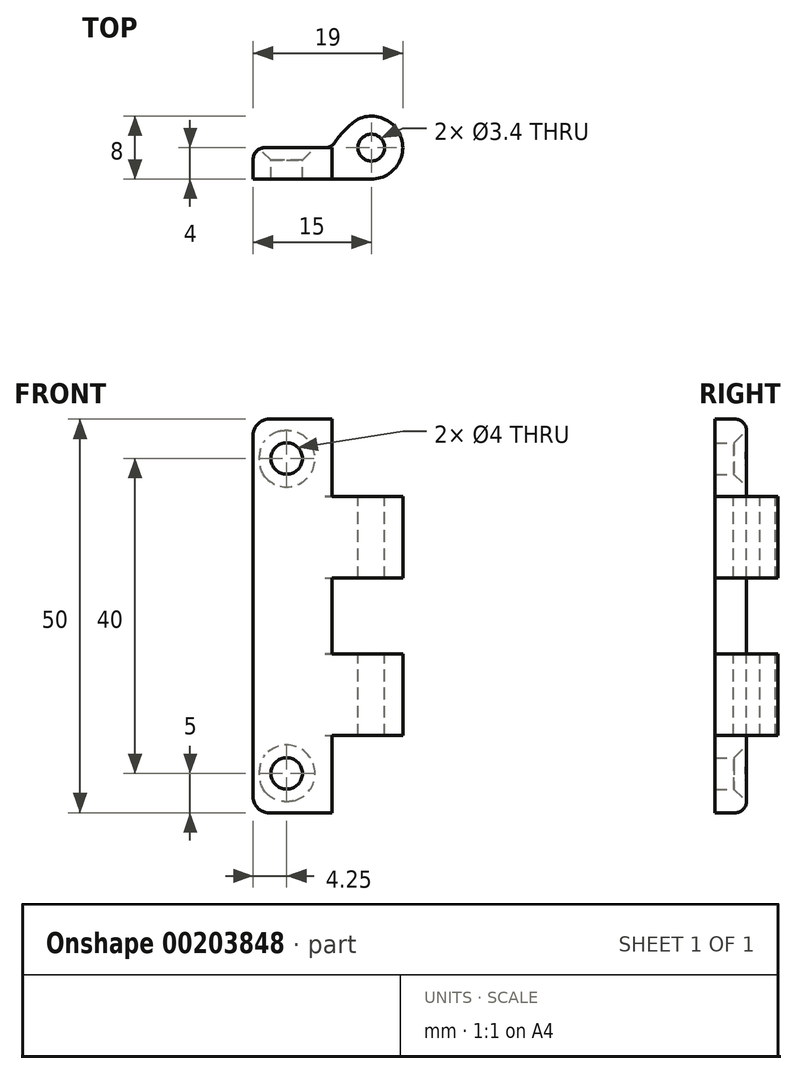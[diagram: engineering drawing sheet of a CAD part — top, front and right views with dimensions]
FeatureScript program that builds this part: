
annotation { "Feature Type Name" : "Feature", "Feature Type Description" : "" }
export const myFeature = defineFeature(function(context is Context, id is Id, definition is map)
    precondition{}
    {
        {
            var Q0;
            Q0=qCreatedBy(makeId("Front.planeOp"),FACE);
            var sketch = newSketch(context, id + "F0", { "sketchPlane" : qUnion([Q0])});
            skLineSegment(sketch, "E0", {"start": v(0, -25) * mm, "end": v(0, 25) * mm});
            skLineSegment(sketch, "E1", {"start": v(-15, -23) * mm, "end": v(-15, 23) * mm});
            skLineSegment(sketch, "E2", {"start": v(-13, 25) * mm, "end": v(0, 25) * mm});
            skLineSegment(sketch, "E3", {"start": v(-13, -25) * mm, "end": v(0, -25) * mm});
            skPoint(sketch, "E4.visualSharp", {"position": v(-15, 25) * mm});
            skArc(sketch, "E4.filletArc", {"start": v(-13, 25) * mm, "mid": v(-14.41, 24.41) * mm, "end": v(-15, 23) * mm});
            skPoint(sketch, "E5.visualSharp", {"position": v(-15, -25) * mm});
            skArc(sketch, "E5.filletArc", {"start": v(-15, -23) * mm, "mid": v(-14.41, -24.41) * mm, "end": v(-13, -25) * mm});
            skCircle(sketch, "E6", {"center": v(-10.75, 20) * mm, "radius": 2 * mm});
            skCircle(sketch, "E7", {"center": v(-10.75, -20) * mm, "radius": 2 * mm});
            skSolve(sketch);
        }
        {
            var Q0;
            Q0 = qSketchRegion(id + "F0", true);
            extrude(context, id + "F1", {"entities" : qUnion([Q0]), "depth" : 4 * mm});
        }
        {
            var Q0;
            Q0=makeQuery(id+"F1.opExtrude","SWEPT_FACE",FACE,{"disambiguationData":[OSD([sQuery(id+"F0.wireOp",EDGE,"E2")])]});
            var sketch = newSketch(context, id + "F2", { "sketchPlane" : qUnion([Q0])});
            skArc(sketch, "E8", {"start": v(-4, 0) * mm, "mid": v(3.46, -2) * mm, "end": v(-2, 3.46) * mm});
            skLineSegment(sketch, "E9", {"start": v(-8, 0) * mm, "end": v(-2, 3.46) * mm});
            skLineSegment(sketch, "E10", {"start": v(-8, 0) * mm, "end": v(-4, 0) * mm});
            skSolve(sketch);
        }
        {
            var Q0;
            Q0 = qSketchRegion(id + "F2", true);
            extrude(context, id + "F3", {"entities" : qUnion([Q0]), "operationType" : NewBodyOperationType.ADD, "oppositeDirection" : true, "depth" : 50 * mm});
        }
        {
            var Q0;
            Q0=makeQuery(id+"F3.boolean.opBoolean","MERGE",FACE,{"derivedFrom":[makeQuery(id+"F1.opExtrude","SWEPT_FACE",FACE,{"disambiguationData":[OSD([sQuery(id+"F0.wireOp",EDGE,"E3")])]}),makeQuery(id+"F3.opExtrude","CAP_FACE",FACE,{"disambiguationData":[OSD([sQuery(id+"F2.wireOp",EDGE,"E8"),sQuery(id+"F2.wireOp",EDGE,"E9"),sQuery(id+"F2.wireOp",EDGE,"E10")])],"isStart":false})]});
            var sketch = newSketch(context, id + "F4", { "sketchPlane" : qUnion([Q0])});
            skLineSegment(sketch, "E11.bottom", {"start": v(-15, 0) * mm, "end": v(-5, 0) * mm});
            skLineSegment(sketch, "E11.top", {"start": v(-15, -3) * mm, "end": v(-5, -3) * mm});
            skLineSegment(sketch, "E11.left", {"start": v(-15, 0) * mm, "end": v(-15, -3) * mm});
            skLineSegment(sketch, "E11.right", {"start": v(-5, 0) * mm, "end": v(-5, -3) * mm});
            skSolve(sketch);
        }
        {
            var Q0;
            Q0 = qSketchRegion(id + "F4", true);
            extrude(context, id + "F5", {"entities" : qUnion([Q0]), "operationType" : NewBodyOperationType.REMOVE, "endBound" : BoundingType.THROUGH_ALL, "oppositeDirection" : true, "depth" : 25 * mm});
        }
        {
            var Q0;
            Q0=makeQuery(id+"F5.boolean.opBoolean","INTERSECT",EDGE,{"derivedFrom":[makeQuery(id+"F3.opExtrude","SWEPT_FACE",FACE,{"disambiguationData":[OSD([sQuery(id+"F2.wireOp",EDGE,"E9")])]}),makeQuery(id+"F5.opExtrude","SWEPT_FACE",FACE,{"disambiguationData":[OSD([sQuery(id+"F4.wireOp",EDGE,"E11.right")])]})]});
            fillet(context, id + "F6", {"entities" : qUnion([Q0]), "radius" : 10 * mm, "tangentPropagation" : true, "allowEdgeOverflow" : false});
        }
        {
            var Q0;
            Q0=makeQuery(id+"F5.boolean.opBoolean","MERGE",FACE,{"derivedFrom":[makeQuery(id+"F1.opExtrude","CAP_FACE",FACE,{"disambiguationData":[OSD([sQuery(id+"F0.wireOp",EDGE,"E0"),sQuery(id+"F0.wireOp",EDGE,"E1"),sQuery(id+"F0.wireOp",EDGE,"E2"),sQuery(id+"F0.wireOp",EDGE,"E3"),sQuery(id+"F0.wireOp",EDGE,"E4.filletArc"),sQuery(id+"F0.wireOp",EDGE,"E5.filletArc"),sQuery(id+"F0.wireOp",EDGE,"E6"),sQuery(id+"F0.wireOp",EDGE,"E7")])],"isStart":true}),makeQuery(id+"F5.opExtrude","SWEPT_FACE",FACE,{"disambiguationData":[OSD([sQuery(id+"F4.wireOp",EDGE,"E11.bottom")])]})]});
            var sketch = newSketch(context, id + "F7", { "sketchPlane" : qUnion([Q0])});
            skLineSegment(sketch, "E12.bottom", {"start": v(5, 25) * mm, "end": v(-5, 25) * mm});
            skLineSegment(sketch, "E12.top", {"start": v(5, 15.2) * mm, "end": v(-5, 15.2) * mm});
            skLineSegment(sketch, "E12.left", {"start": v(5, 25) * mm, "end": v(5, 15.2) * mm});
            skLineSegment(sketch, "E12.right", {"start": v(-5, 25) * mm, "end": v(-5, 15.2) * mm});
            skLineSegment(sketch, "E13.bottom", {"start": v(5, -25) * mm, "end": v(-5, -25) * mm});
            skLineSegment(sketch, "E13.top", {"start": v(5, -15.2) * mm, "end": v(-5, -15.2) * mm});
            skLineSegment(sketch, "E13.left", {"start": v(5, -25) * mm, "end": v(5, -15.2) * mm});
            skLineSegment(sketch, "E13.right", {"start": v(-5, -25) * mm, "end": v(-5, -15.2) * mm});
            skLineSegment(sketch, "E14.bottom", {"start": v(5, -4.8) * mm, "end": v(-5, -4.8) * mm});
            skLineSegment(sketch, "E14.top", {"start": v(5, 4.8) * mm, "end": v(-5, 4.8) * mm});
            skLineSegment(sketch, "E14.left", {"start": v(5, -4.8) * mm, "end": v(5, 4.8) * mm});
            skLineSegment(sketch, "E14.right", {"start": v(-5, -4.8) * mm, "end": v(-5, 4.8) * mm});
            skLineSegment(sketch, "E15", {"start": v(0, 0) * mm, "end": v(5, 0) * mm, "construction": true});
            skSolve(sketch);
        }
        {
            var Q0;
            Q0=makeQuery(id+"F7.imprint","IMPRINT",FACE,{"disambiguationData":[TD([[makeQuery(id+"F7.imprint","IMPRINT",EDGE,{"derivedFrom":sQuery(id+"F7.wireOp",EDGE,"E12.bottom")}),1.0]])]});
            var Q1;
            Q1=makeQuery(id+"F7.imprint","IMPRINT",FACE,{"disambiguationData":[TD([[makeQuery(id+"F7.imprint","IMPRINT",EDGE,{"derivedFrom":sQuery(id+"F7.wireOp",EDGE,"E13.bottom")}),-1.0]])]});
            var Q2;
            Q2=makeQuery(id+"F7.imprint","IMPRINT",FACE,{"disambiguationData":[TD([[makeQuery(id+"F7.imprint","IMPRINT",EDGE,{"derivedFrom":sQuery(id+"F7.wireOp",EDGE,"E14.bottom")}),-1.0]])]});
            var Q3;
            Q3=sQuery(id+"F7.wireOp",EDGE,"E14.top");
            var Q4;
            Q4=sQuery(id+"F7.wireOp",EDGE,"E12.top");
            var Q5;
            Q5=sQuery(id+"F7.wireOp",EDGE,"E13.top");
            var Q6;
            Q6=sQuery(id+"F7.wireOp",EDGE,"E14.bottom");
            var Q7;
            Q7=sQuery(id+"F7.wireOp",EDGE,"E14.right");
            var Q8;
            Q8=sQuery(id+"F7.wireOp",EDGE,"E14.left");
            var Q9;
            Q9=sQuery(id+"F7.wireOp",EDGE,"E12.left");
            var Q10;
            Q10=sQuery(id+"F7.wireOp",EDGE,"E12.bottom");
            var Q11;
            Q11=sQuery(id+"F7.wireOp",EDGE,"E12.right");
            var Q12;
            Q12=sQuery(id+"F7.wireOp",EDGE,"E13.right");
            var Q13;
            Q13=sQuery(id+"F7.wireOp",EDGE,"E13.bottom");
            var Q14;
            Q14=sQuery(id+"F7.wireOp",EDGE,"E13.left");
            extrude(context, id + "F8", {"entities" : qUnion([Q0, Q1, Q2]), "operationType" : NewBodyOperationType.REMOVE, "surfaceEntities" : qUnion([Q3, Q4, Q5, Q6, Q7, Q8, Q9, Q10, Q11, Q12, Q13, Q14]), "endBound" : BoundingType.SYMMETRIC, "oppositeDirection" : true, "depth" : 25 * mm});
        }
        {
            var Q0;
            Q0=makeQuery(id+"F8.boolean.opBoolean","COPY",FACE,{"derivedFrom":makeQuery(id+"F8.opExtrude","SWEPT_FACE",FACE,{"disambiguationData":[OSD([sQuery(id+"F7.wireOp",EDGE,"E12.top")])]})});
            var sketch = newSketch(context, id + "F9", { "sketchPlane" : qUnion([Q0])});
            skCircle(sketch, "E16", {"center": v(0, 0) * mm, "radius": 1.7 * mm});
            skSolve(sketch);
        }
        {
            var Q0;
            Q0=makeQuery(id+"F1.opExtrude","CAP_EDGE",EDGE,{"disambiguationData":[OSD([sQuery(id+"F0.wireOp",EDGE,"E7")])],"isStart":true});
            var Q1;
            Q1=makeQuery(id+"F1.opExtrude","CAP_EDGE",EDGE,{"disambiguationData":[OSD([sQuery(id+"F0.wireOp",EDGE,"E6")])],"isStart":true});
            chamfer(context, id + "F10", {"entities" : qUnion([Q0, Q1]), "width" : 1.6 * mm, "tangentPropagation" : true});
        }
        {
            var Q0;
            {var subQ0=sQuery(id+"F4.wireOp",EDGE,"E11.right");var subQ1=sQuery(id+"F2.wireOp",EDGE,"E9");var subQ2=makeQuery(id+"F5.opExtrude","SWEPT_FACE",FACE,{"disambiguationData":[OSD([sQuery(id+"F4.wireOp",EDGE,"E11.bottom")])]});var subQ3=makeQuery(id+"F1.opExtrude","CAP_FACE",FACE,{"disambiguationData":[OSD([sQuery(id+"F0.wireOp",EDGE,"E0"),sQuery(id+"F0.wireOp",EDGE,"E1"),sQuery(id+"F0.wireOp",EDGE,"E2"),sQuery(id+"F0.wireOp",EDGE,"E3"),sQuery(id+"F0.wireOp",EDGE,"E4.filletArc"),sQuery(id+"F0.wireOp",EDGE,"E5.filletArc"),sQuery(id+"F0.wireOp",EDGE,"E6"),sQuery(id+"F0.wireOp",EDGE,"E7")])],"isStart":true});Q0=makeQuery(id+"F8.boolean.opBoolean","SPLIT",EDGE,{"disambiguationData":[TD([subQ3,subQ2,makeQuery(id+"F6.opFillet","BLEND_FACE",FACE,{"disambiguationData":[OSD([subQ1,subQ0])]}),makeQuery(id+"F8.opExtrude","SWEPT_FACE",FACE,{"disambiguationData":[OSD([sQuery(id+"F7.wireOp",EDGE,"E14.bottom")])]}),makeQuery(id+"F8.opExtrude","SWEPT_FACE",FACE,{"disambiguationData":[OSD([sQuery(id+"F7.wireOp",EDGE,"E14.top")])]}),makeQuery(id+"F8.opExtrude","SWEPT_FACE",FACE,{"disambiguationData":[OSD([sQuery(id+"F7.wireOp",EDGE,"E14.left")])]})])],"derivedFrom":makeQuery(id+"F6.opFillet","BLEND_EDGE",EDGE,{"blendedFrom":[makeQuery(id+"F5.boolean.opBoolean","INTERSECT",EDGE,{"derivedFrom":[makeQuery(id+"F3.opExtrude","SWEPT_FACE",FACE,{"disambiguationData":[OSD([subQ1])]}),makeQuery(id+"F5.opExtrude","SWEPT_FACE",FACE,{"disambiguationData":[OSD([subQ0])]})]}),makeQuery(id+"F5.boolean.opBoolean","MERGE",FACE,{"derivedFrom":[subQ3,subQ2]})],"blendedInto":[makeQuery(id+"F5.boolean.opBoolean","MERGE",FACE,{"derivedFrom":[subQ3,subQ2]})]})});}
            var Q1;
            Q1=makeQuery(id+"F5.boolean.opBoolean","INTERSECT",EDGE,{"derivedFrom":[makeQuery(id+"F3.boolean.opBoolean","MERGE",FACE,{"derivedFrom":[makeQuery(id+"F1.opExtrude","SWEPT_FACE",FACE,{"disambiguationData":[OSD([sQuery(id+"F0.wireOp",EDGE,"E2")])]}),makeQuery(id+"F3.opExtrude","CAP_FACE",FACE,{"disambiguationData":[OSD([sQuery(id+"F2.wireOp",EDGE,"E8"),sQuery(id+"F2.wireOp",EDGE,"E9"),sQuery(id+"F2.wireOp",EDGE,"E10")])],"isStart":true})]}),makeQuery(id+"F5.opExtrude","SWEPT_FACE",FACE,{"disambiguationData":[OSD([sQuery(id+"F4.wireOp",EDGE,"E11.bottom")])]})]});
            var Q2;
            {var subQ0=makeQuery(id+"F5.opExtrude","SWEPT_FACE",FACE,{"disambiguationData":[OSD([sQuery(id+"F4.wireOp",EDGE,"E11.bottom")])]});var subQ1=sQuery(id+"F0.wireOp",EDGE,"E2");var subQ2=sQuery(id+"F2.wireOp",EDGE,"E9");var subQ3=makeQuery(id+"F1.opExtrude","CAP_FACE",FACE,{"disambiguationData":[OSD([sQuery(id+"F0.wireOp",EDGE,"E0"),sQuery(id+"F0.wireOp",EDGE,"E1"),subQ1,sQuery(id+"F0.wireOp",EDGE,"E3"),sQuery(id+"F0.wireOp",EDGE,"E4.filletArc"),sQuery(id+"F0.wireOp",EDGE,"E5.filletArc"),sQuery(id+"F0.wireOp",EDGE,"E6"),sQuery(id+"F0.wireOp",EDGE,"E7")])],"isStart":true});var subQ4=sQuery(id+"F4.wireOp",EDGE,"E11.right");Q2=makeQuery(id+"F8.boolean.opBoolean","SPLIT",EDGE,{"disambiguationData":[TD([subQ3,makeQuery(id+"F1.opExtrude","SWEPT_FACE",FACE,{"disambiguationData":[OSD([subQ1])]}),makeQuery(id+"F3.opExtrude","CAP_FACE",FACE,{"disambiguationData":[OSD([sQuery(id+"F2.wireOp",EDGE,"E8"),subQ2,sQuery(id+"F2.wireOp",EDGE,"E10")])],"isStart":true}),subQ0,makeQuery(id+"F6.opFillet","BLEND_FACE",FACE,{"disambiguationData":[OSD([subQ2,subQ4])]}),makeQuery(id+"F8.opExtrude","SWEPT_FACE",FACE,{"disambiguationData":[OSD([sQuery(id+"F7.wireOp",EDGE,"E12.top")])]}),makeQuery(id+"F8.opExtrude","SWEPT_FACE",FACE,{"disambiguationData":[OSD([sQuery(id+"F7.wireOp",EDGE,"E12.left")])]})])],"derivedFrom":makeQuery(id+"F6.opFillet","BLEND_EDGE",EDGE,{"blendedFrom":[makeQuery(id+"F5.boolean.opBoolean","INTERSECT",EDGE,{"derivedFrom":[makeQuery(id+"F3.opExtrude","SWEPT_FACE",FACE,{"disambiguationData":[OSD([subQ2])]}),makeQuery(id+"F5.opExtrude","SWEPT_FACE",FACE,{"disambiguationData":[OSD([subQ4])]})]}),makeQuery(id+"F5.boolean.opBoolean","MERGE",FACE,{"derivedFrom":[subQ3,subQ0]})],"blendedInto":[makeQuery(id+"F5.boolean.opBoolean","MERGE",FACE,{"derivedFrom":[subQ3,subQ0]})]})});}
            var Q3;
            {var subQ0=makeQuery(id+"F5.opExtrude","SWEPT_FACE",FACE,{"disambiguationData":[OSD([sQuery(id+"F4.wireOp",EDGE,"E11.bottom")])]});var subQ1=sQuery(id+"F0.wireOp",EDGE,"E3");var subQ2=sQuery(id+"F2.wireOp",EDGE,"E9");var subQ3=makeQuery(id+"F1.opExtrude","CAP_FACE",FACE,{"disambiguationData":[OSD([sQuery(id+"F0.wireOp",EDGE,"E0"),sQuery(id+"F0.wireOp",EDGE,"E1"),sQuery(id+"F0.wireOp",EDGE,"E2"),subQ1,sQuery(id+"F0.wireOp",EDGE,"E4.filletArc"),sQuery(id+"F0.wireOp",EDGE,"E5.filletArc"),sQuery(id+"F0.wireOp",EDGE,"E6"),sQuery(id+"F0.wireOp",EDGE,"E7")])],"isStart":true});var subQ4=sQuery(id+"F4.wireOp",EDGE,"E11.right");Q3=makeQuery(id+"F8.boolean.opBoolean","SPLIT",EDGE,{"disambiguationData":[TD([subQ3,makeQuery(id+"F1.opExtrude","SWEPT_FACE",FACE,{"disambiguationData":[OSD([subQ1])]}),makeQuery(id+"F3.opExtrude","CAP_FACE",FACE,{"disambiguationData":[OSD([sQuery(id+"F2.wireOp",EDGE,"E8"),subQ2,sQuery(id+"F2.wireOp",EDGE,"E10")])],"isStart":false}),subQ0,makeQuery(id+"F6.opFillet","BLEND_FACE",FACE,{"disambiguationData":[OSD([subQ2,subQ4])]}),makeQuery(id+"F8.opExtrude","SWEPT_FACE",FACE,{"disambiguationData":[OSD([sQuery(id+"F7.wireOp",EDGE,"E13.top")])]}),makeQuery(id+"F8.opExtrude","SWEPT_FACE",FACE,{"disambiguationData":[OSD([sQuery(id+"F7.wireOp",EDGE,"E13.left")])]})])],"derivedFrom":makeQuery(id+"F6.opFillet","BLEND_EDGE",EDGE,{"blendedFrom":[makeQuery(id+"F5.boolean.opBoolean","INTERSECT",EDGE,{"derivedFrom":[makeQuery(id+"F3.opExtrude","SWEPT_FACE",FACE,{"disambiguationData":[OSD([subQ2])]}),makeQuery(id+"F5.opExtrude","SWEPT_FACE",FACE,{"disambiguationData":[OSD([subQ4])]})]}),makeQuery(id+"F5.boolean.opBoolean","MERGE",FACE,{"derivedFrom":[subQ3,subQ0]})],"blendedInto":[makeQuery(id+"F5.boolean.opBoolean","MERGE",FACE,{"derivedFrom":[subQ3,subQ0]})]})});}
            var Q4;
            Q4=makeQuery(id+"F8.boolean.opBoolean","COPY",EDGE,{"derivedFrom":makeQuery(id+"F8.opExtrude","SWEPT_EDGE",EDGE,{"disambiguationData":[OSD([sQuery(id+"F0.wireOp",EDGE,"E2"),sQuery(id+"F2.wireOp",EDGE,"E8"),sQuery(id+"F2.wireOp",EDGE,"E9"),sQuery(id+"F2.wireOp",EDGE,"E10"),sQuery(id+"F4.wireOp",EDGE,"E11.bottom"),sQuery(id+"F7.wireOp",EDGE,"E12.bottom"),sQuery(id+"F7.wireOp",EDGE,"E12.left")])]})});
            var Q5;
            Q5=makeQuery(id+"F8.boolean.opBoolean","COPY",EDGE,{"derivedFrom":makeQuery(id+"F8.opExtrude","SWEPT_EDGE",EDGE,{"disambiguationData":[OSD([sQuery(id+"F0.wireOp",EDGE,"E3"),sQuery(id+"F4.wireOp",EDGE,"E11.bottom"),sQuery(id+"F7.wireOp",EDGE,"E13.bottom"),sQuery(id+"F7.wireOp",EDGE,"E13.left")])]})});
            fillet(context, id + "F11", {"entities" : qUnion([Q0, Q1, Q2, Q3, Q4, Q5]), "radius" : 1.5 * mm, "tangentPropagation" : true, "allowEdgeOverflow" : false});
        }
        {
            var Q0;
            Q0 = qSketchRegion(id + "F9", true);
            extrude(context, id + "F12", {"entities" : qUnion([Q0]), "operationType" : NewBodyOperationType.REMOVE, "endBound" : BoundingType.THROUGH_ALL, "oppositeDirection" : true, "depth" : 25 * mm});
        }
    });
